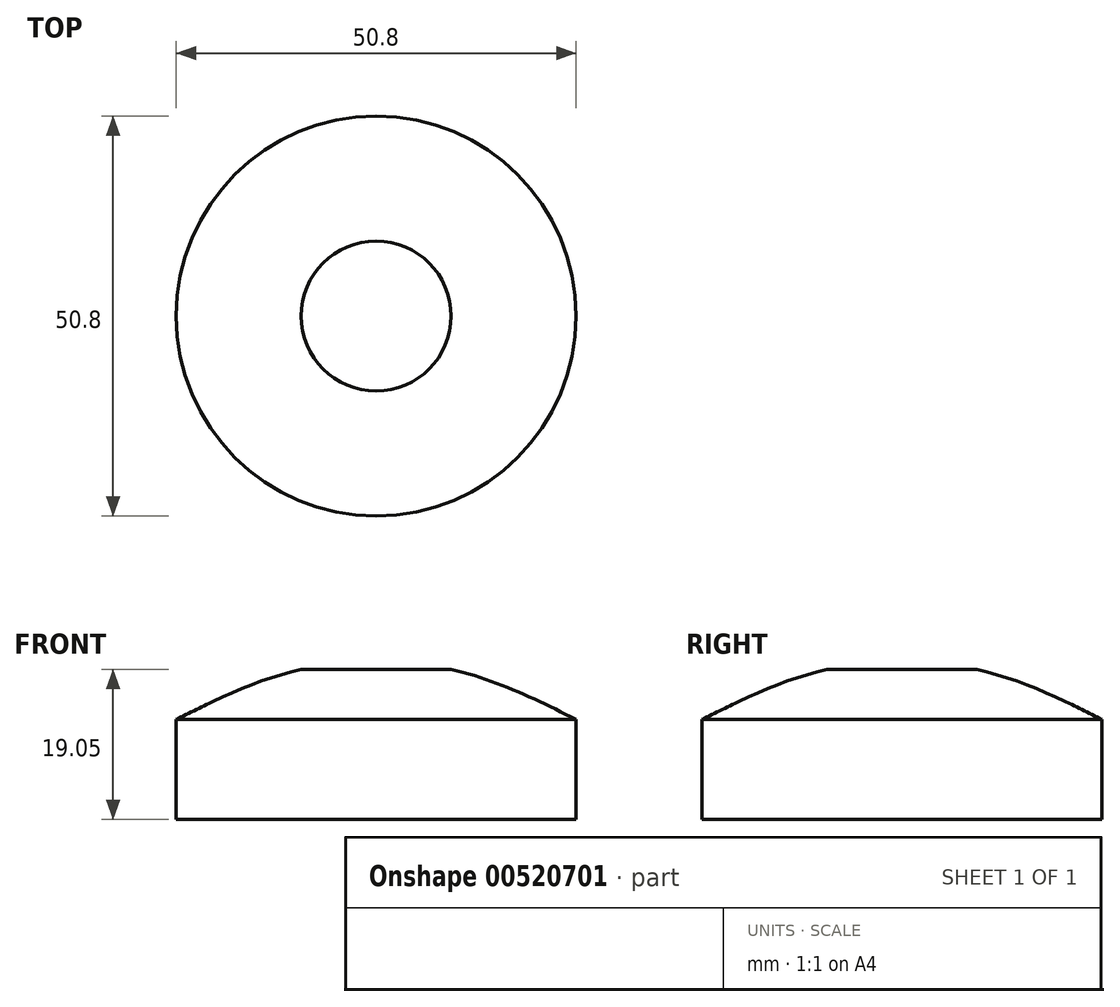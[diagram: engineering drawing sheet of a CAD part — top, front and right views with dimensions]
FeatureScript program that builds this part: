
annotation { "Feature Type Name" : "Feature", "Feature Type Description" : "" }
export const myFeature = defineFeature(function(context is Context, id is Id, definition is map)
    precondition{}
    {
        {
            var Q0;
            Q0=qCreatedBy(makeId("Top.planeOp"),FACE);
            var sketch = newSketch(context, id + "F0", { "sketchPlane" : qUnion([Q0])});
            skCircle(sketch, "E0", {"center": v(0, 0) * mm, "radius": 25.4 * mm});
            skSolve(sketch);
        }
        {
            var Q0;
            Q0 = qSketchRegion(id + "F0", true);
            extrude(context, id + "F1", {"entities" : qUnion([Q0]), "depth" : 12.7 * mm, "offsetDistance" : 25.4 * mm});
        }
        {
            var Q0;
            Q0=qCreatedBy(makeId("Front.planeOp"),FACE);
            var sketch = newSketch(context, id + "F2", { "sketchPlane" : qUnion([Q0])});
            skLineSegment(sketch, "E1.bottom", {"start": v(-25.4, 12.7) * mm, "end": v(-9.53, 12.7) * mm});
            skLineSegment(sketch, "E2.bottom", {"start": v(-9.53, 19.05) * mm, "end": v(0, 19.05) * mm});
            skPoint(sketch, "E2.middle", {"position": v(0, 12.7) * mm});
            skFitSpline(sketch, "E3", {"points": [v(-25.4, 12.7) * mm, v(-9.53, 19.05) * mm, v(9.53, 19.05) * mm, v(25.4, 12.7) * mm], "startDerivative": vector(46.33, 23.16) * mm, "endDerivative": vector(46.33, -23.16) * mm});
            skPoint(sketch, "E4", {"position": v(0, 19.05) * mm});
            skLineSegment(sketch, "E5", {"start": v(0, 19.05) * mm, "end": v(0, 12.7) * mm});
            skLineSegment(sketch, "E6", {"start": v(-9.53, 12.7) * mm, "end": v(0, 12.7) * mm});
            skSolve(sketch);
        }
        {
            var Q0;
            Q0 = qSketchRegion(id + "F2", true);
            var Q1;
            Q1=sQuery(id+"F2.wireOp",EDGE,"E5");
            revolve(context, id + "F3", {"entities" : qUnion([Q0]), "axis" : qUnion([Q1]), "revolveType" : RevolveType.FULL});
        }
    });
